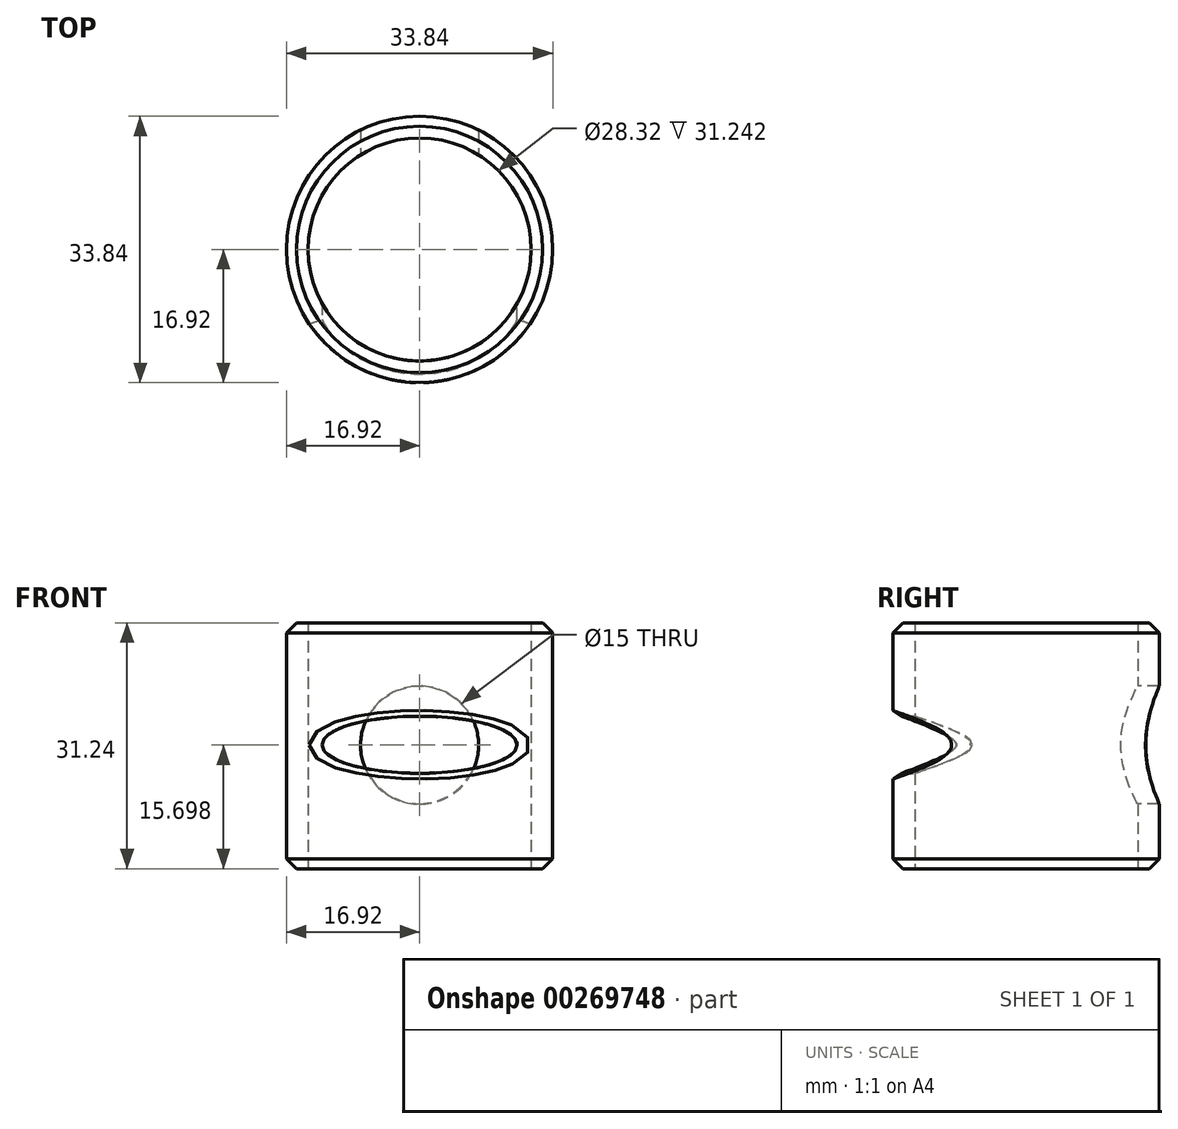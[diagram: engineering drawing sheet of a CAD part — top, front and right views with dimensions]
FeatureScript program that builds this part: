
annotation { "Feature Type Name" : "Feature", "Feature Type Description" : "" }
export const myFeature = defineFeature(function(context is Context, id is Id, definition is map)
    precondition{}
    {
        {
            var Q0;
            Q0=qCreatedBy(makeId("Top.planeOp"),FACE);
            var sketch = newSketch(context, id + "F0", { "sketchPlane" : qUnion([Q0])});
            skCircle(sketch, "E0", {"center": v(0, 0) * mm, "radius": 16.92 * mm});
            skCircle(sketch, "E1", {"center": v(0, 0) * mm, "radius": 14.16 * mm});
            skSolve(sketch);
        }
        {
            var Q0;
            Q0 = qSketchRegion(id + "F0", true);
            extrude(context, id + "F1", {"entities" : qUnion([Q0]), "depth" : 31.24 * mm});
        }
        {
            var Q0;
            Q0=makeQuery(id+"F1.opExtrude","CAP_EDGE",EDGE,{"disambiguationData":[OSD([sQuery(id+"F0.wireOp",EDGE,"E0")])],"isStart":true});
            var Q1;
            Q1=makeQuery(id+"F1.opExtrude","CAP_EDGE",EDGE,{"disambiguationData":[OSD([sQuery(id+"F0.wireOp",EDGE,"E0")])],"isStart":false});
            chamfer(context, id + "F2", {"entities" : qUnion([Q0, Q1]), "width" : 1.27 * mm, "tangentPropagation" : true});
        }
        {
            var Q0;
            Q0=qCreatedBy(makeId("Front.planeOp"),FACE);
            var sketch = newSketch(context, id + "F3", { "sketchPlane" : qUnion([Q0])});
            skCircle(sketch, "E2", {"center": v(0, 15.7) * mm, "radius": 7.5 * mm});
            skSolve(sketch);
        }
        {
            var Q0;
            Q0 = qSketchRegion(id + "F3", true);
            extrude(context, id + "F4", {"entities" : qUnion([Q0]), "operationType" : NewBodyOperationType.REMOVE, "oppositeDirection" : true, "depth" : 25.4 * mm});
        }
        {
            var Q0;
            Q0=qCreatedBy(makeId("Front.planeOp"),FACE);
            var sketch = newSketch(context, id + "F5", { "sketchPlane" : qUnion([Q0])});
            skEllipse(sketch, "E3", {"center": v(0, 15.74) * mm, "majorRadius": 12.4 * mm, "minorRadius": 3.62 * mm, "majorAxis": v(1, 0)});
            skSolve(sketch);
        }
        {
            var Q0;
            Q0 = qSketchRegion(id + "F5", true);
            extrude(context, id + "F6", {"entities" : qUnion([Q0]), "operationType" : NewBodyOperationType.REMOVE, "depth" : 33.53 * mm});
        }
        {
            var Q0;
            Q0=makeQuery(id+"F6.boolean.opBoolean","INTERSECT",EDGE,{"derivedFrom":[makeQuery(id+"F1.opExtrude","SWEPT_FACE",FACE,{"disambiguationData":[OSD([sQuery(id+"F0.wireOp",EDGE,"E0")])]}),makeQuery(id+"F6.opExtrude","SWEPT_FACE",FACE,{"disambiguationData":[OSD([sQuery(id+"F5.wireOp",EDGE,"E3")])]})]});
            chamfer(context, id + "F7", {"entities" : qUnion([Q0]), "width" : 2.54 * mm, "tangentPropagation" : true});
        }
    });
